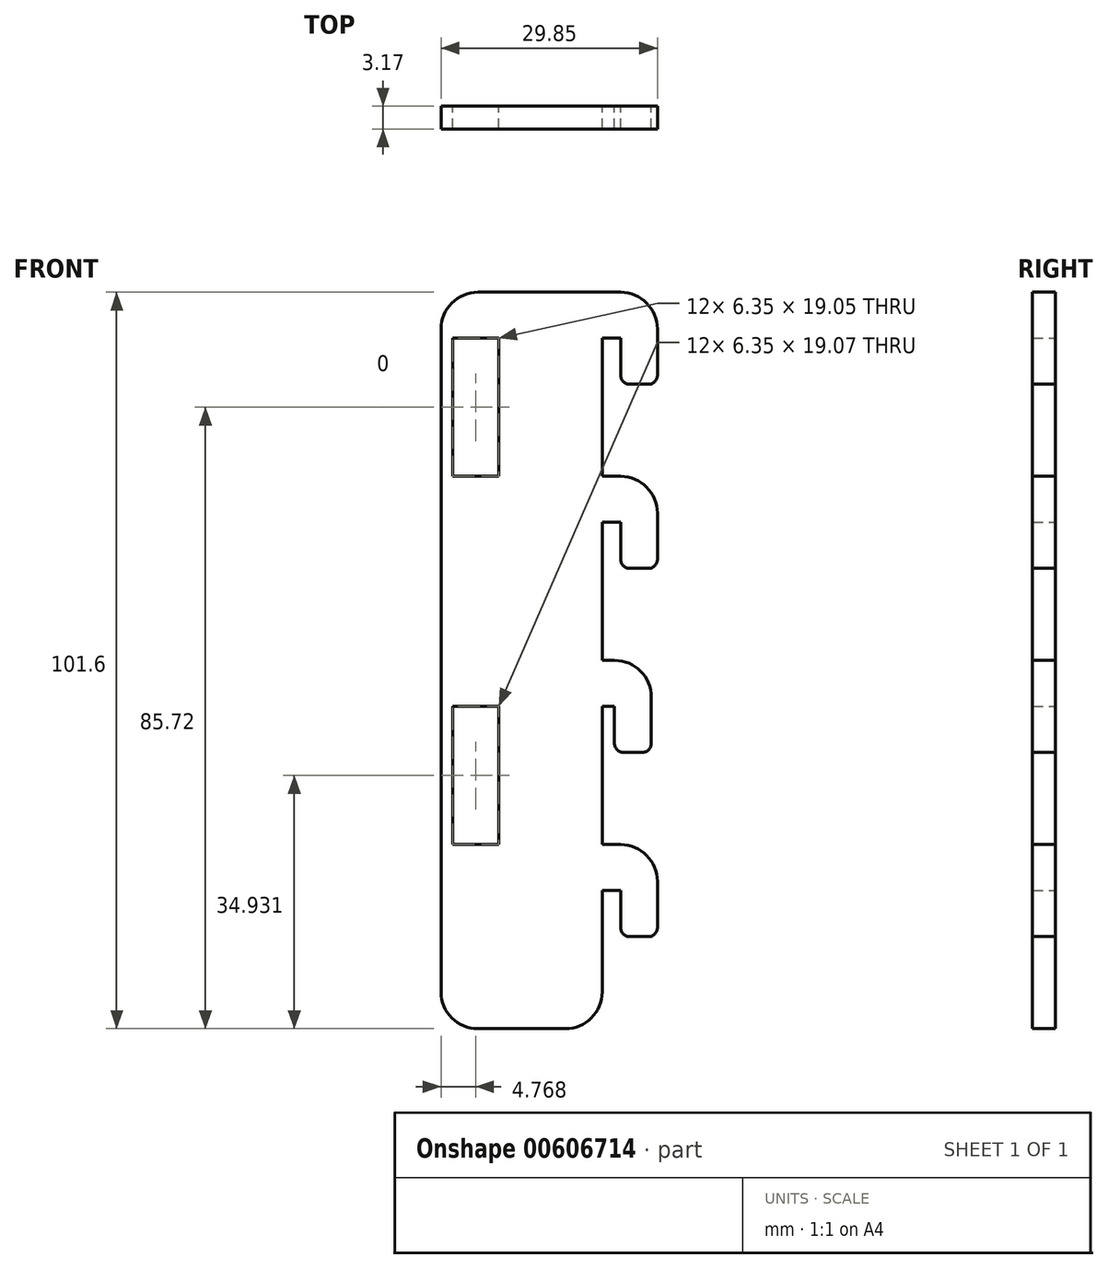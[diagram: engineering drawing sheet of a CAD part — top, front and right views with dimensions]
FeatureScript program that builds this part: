
annotation { "Feature Type Name" : "Feature", "Feature Type Description" : "" }
export const myFeature = defineFeature(function(context is Context, id is Id, definition is map)
    precondition{}
    {
        {
            var Q0;
            Q0=qCreatedBy(makeId("Front.planeOp"),FACE);
            var sketch = newSketch(context, id + "F0", { "sketchPlane" : qUnion([Q0])});
            skLineSegment(sketch, "E0", {"start": v(0, 56.94) * mm, "end": v(0, -44.66) * mm});
            skLineSegment(sketch, "E1", {"start": v(0, 56.94) * mm, "end": v(7.62, 56.94) * mm});
            skLineSegment(sketch, "E2", {"start": v(7.62, 56.94) * mm, "end": v(7.62, 44.24) * mm});
            skLineSegment(sketch, "E3", {"start": v(7.62, 44.24) * mm, "end": v(2.54, 44.24) * mm});
            skLineSegment(sketch, "E4", {"start": v(2.54, 44.24) * mm, "end": v(2.54, 50.59) * mm});
            skLineSegment(sketch, "E5", {"start": v(2.54, 50.59) * mm, "end": v(0, 50.59) * mm});
            skLineSegment(sketch, "E6", {"start": v(0, 56.94) * mm, "end": v(-12.7, 56.94) * mm});
            skLineSegment(sketch, "E7", {"start": v(-12.7, 56.94) * mm, "end": v(-12.7, -44.66) * mm});
            skLineSegment(sketch, "E8", {"start": v(-12.7, -44.66) * mm, "end": v(0, -44.66) * mm});
            skLineSegment(sketch, "E9", {"start": v(0, 56.94) * mm, "end": v(0, 31.54) * mm});
            skLineSegment(sketch, "E10", {"start": v(0, 31.54) * mm, "end": v(7.62, 31.54) * mm});
            skLineSegment(sketch, "E11", {"start": v(7.62, 31.54) * mm, "end": v(7.62, 18.84) * mm});
            skLineSegment(sketch, "E12", {"start": v(7.62, 18.84) * mm, "end": v(2.54, 18.84) * mm});
            skLineSegment(sketch, "E13", {"start": v(2.54, 18.84) * mm, "end": v(2.54, 25.19) * mm});
            skLineSegment(sketch, "E14", {"start": v(2.54, 25.19) * mm, "end": v(0, 25.19) * mm});
            skLineSegment(sketch, "E15", {"start": v(0, 31.54) * mm, "end": v(0, 0) * mm});
            skLineSegment(sketch, "E16", {"start": v(0, 31.54) * mm, "end": v(0, 6.14) * mm});
            skLineSegment(sketch, "E17", {"start": v(0, 6.14) * mm, "end": v(0, -19.26) * mm});
            skLineSegment(sketch, "E18", {"start": v(0, -19.26) * mm, "end": v(0, -44.66) * mm});
            skLineSegment(sketch, "E19", {"start": v(-0.85, 6.16) * mm, "end": v(6.77, 6.16) * mm});
            skLineSegment(sketch, "E20", {"start": v(6.77, 6.16) * mm, "end": v(6.77, -6.54) * mm});
            skLineSegment(sketch, "E21", {"start": v(6.77, -6.54) * mm, "end": v(1.7, -6.54) * mm});
            skLineSegment(sketch, "E22", {"start": v(1.7, -6.54) * mm, "end": v(1.7, -0.2) * mm});
            skLineSegment(sketch, "E23", {"start": v(1.7, -0.2) * mm, "end": v(-0.85, -0.2) * mm});
            skLineSegment(sketch, "E24", {"start": v(0, -19.26) * mm, "end": v(7.62, -19.26) * mm});
            skLineSegment(sketch, "E25", {"start": v(7.62, -19.26) * mm, "end": v(7.62, -31.96) * mm});
            skLineSegment(sketch, "E26", {"start": v(7.62, -31.96) * mm, "end": v(2.54, -31.96) * mm});
            skLineSegment(sketch, "E27", {"start": v(2.54, -31.96) * mm, "end": v(2.54, -25.61) * mm});
            skLineSegment(sketch, "E28", {"start": v(2.54, -25.61) * mm, "end": v(0, -25.61) * mm});
            skLineSegment(sketch, "E29", {"start": v(-12.7, 56.94) * mm, "end": v(-22.22, 56.94) * mm});
            skLineSegment(sketch, "E30", {"start": v(-22.22, 56.94) * mm, "end": v(-22.22, -44.66) * mm});
            skLineSegment(sketch, "E31", {"start": v(-22.22, -44.66) * mm, "end": v(-12.7, -44.66) * mm});
            skLineSegment(sketch, "E32", {"start": v(-17.46, -44.66) * mm, "end": v(-17.46, 56.94) * mm});
            skPoint(sketch, "E32.startSnap0", {"position": v(-17.46, 56.94) * mm});
            skLineSegment(sketch, "E33", {"start": v(-17.46, 50.59) * mm, "end": v(-14.29, 50.59) * mm});
            skLineSegment(sketch, "E34", {"start": v(-14.29, 50.59) * mm, "end": v(-14.29, 31.54) * mm});
            skLineSegment(sketch, "E35", {"start": v(-14.29, 31.54) * mm, "end": v(-20.64, 31.54) * mm});
            skLineSegment(sketch, "E36", {"start": v(-20.64, 31.54) * mm, "end": v(-20.64, 50.59) * mm});
            skLineSegment(sketch, "E37", {"start": v(-20.64, 50.59) * mm, "end": v(-17.46, 50.59) * mm});
            skLineSegment(sketch, "E38", {"start": v(-20.64, -0.2) * mm, "end": v(-14.29, -0.2) * mm});
            skPoint(sketch, "E38.endSnap0", {"position": v(0.42, -0.2) * mm});
            skLineSegment(sketch, "E39", {"start": v(-14.29, -0.2) * mm, "end": v(-14.29, -19.26) * mm});
            skLineSegment(sketch, "E40", {"start": v(-14.29, -19.26) * mm, "end": v(-20.64, -19.24) * mm});
            skLineSegment(sketch, "E41", {"start": v(-20.64, -19.24) * mm, "end": v(-20.64, -0.2) * mm});
            skSolve(sketch);
        }
        {
            var Q0;
            {var subQ7=sQuery(id+"F0.wireOp",EDGE,"E6");Q0=makeQuery(id+"F0.imprint","IMPRINT",FACE,{"disambiguationData":[TD([[makeQuery(id+"F0.imprint","IMPRINT",EDGE,{"derivedFrom":subQ7}),1.0]])]});}
            var Q1;
            {var subQ0=sQuery(id+"F0.wireOp",EDGE,"E1");Q1=makeQuery(id+"F0.imprint","IMPRINT",FACE,{"disambiguationData":[TD([[makeQuery(id+"F0.imprint","IMPRINT",EDGE,{"derivedFrom":subQ0}),-1.0]])]});}
            var Q2;
            {var subQ0=sQuery(id+"F0.wireOp",EDGE,"E10");Q2=makeQuery(id+"F0.imprint","IMPRINT",FACE,{"disambiguationData":[TD([[makeQuery(id+"F0.imprint","IMPRINT",EDGE,{"derivedFrom":subQ0}),-1.0]])]});}
            var Q3;
            {var subQ0=sQuery(id+"F0.wireOp",EDGE,"E20");Q3=makeQuery(id+"F0.imprint","IMPRINT",FACE,{"disambiguationData":[TD([[makeQuery(id+"F0.imprint","IMPRINT",EDGE,{"derivedFrom":subQ0}),-1.0]])]});}
            var Q4;
            {var subQ0=sQuery(id+"F0.wireOp",EDGE,"E24");Q4=makeQuery(id+"F0.imprint","IMPRINT",FACE,{"disambiguationData":[TD([[makeQuery(id+"F0.imprint","IMPRINT",EDGE,{"derivedFrom":subQ0}),-1.0]])]});}
            var Q5;
            {var subQ8=sQuery(id+"F0.wireOp",EDGE,"E7");Q5=makeQuery(id+"F0.imprint","IMPRINT",FACE,{"disambiguationData":[TD([[makeQuery(id+"F0.imprint","IMPRINT",EDGE,{"derivedFrom":subQ8}),-1.0]])]});}
            var Q6;
            {var subQ10=sQuery(id+"F0.wireOp",EDGE,"E30");Q6=makeQuery(id+"F0.imprint","IMPRINT",FACE,{"disambiguationData":[TD([[makeQuery(id+"F0.imprint","IMPRINT",EDGE,{"derivedFrom":subQ10}),1.0]])]});}
            extrude(context, id + "F1", {"entities" : qUnion([Q0, Q1, Q2, Q3, Q4, Q5, Q6]), "depth" : 3.17 * mm, "offsetDistance" : 25.4 * mm});
        }
        {
            var Q0;
            Q0=makeQuery(id+"F1.opExtrude","SWEPT_EDGE",EDGE,{"disambiguationData":[OSD([sQuery(id+"F0.wireOp",EDGE,"E29"),sQuery(id+"F0.wireOp",EDGE,"E30")])]});
            var Q1;
            Q1=makeQuery(id+"F1.opExtrude","SWEPT_EDGE",EDGE,{"disambiguationData":[OSD([sQuery(id+"F0.wireOp",EDGE,"E30"),sQuery(id+"F0.wireOp",EDGE,"E31")])]});
            var Q2;
            Q2=makeQuery(id+"F1.opExtrude","SWEPT_EDGE",EDGE,{"disambiguationData":[OSD([sQuery(id+"F0.wireOp",EDGE,"E8"),sQuery(id+"F0.wireOp",EDGE,"E18")])]});
            fillet(context, id + "F2", {"entities" : qUnion([Q0, Q1, Q2]), "radius" : 5.08 * mm, "tangentPropagation" : true, "allowEdgeOverflow" : false});
        }
        {
            var Q0;
            Q0=makeQuery(id+"F1.opExtrude","SWEPT_EDGE",EDGE,{"disambiguationData":[OSD([sQuery(id+"F0.wireOp",EDGE,"E10"),sQuery(id+"F0.wireOp",EDGE,"E11")])]});
            var Q1;
            Q1=makeQuery(id+"F1.opExtrude","SWEPT_EDGE",EDGE,{"disambiguationData":[OSD([sQuery(id+"F0.wireOp",EDGE,"E19"),sQuery(id+"F0.wireOp",EDGE,"E20")])]});
            var Q2;
            Q2=makeQuery(id+"F1.opExtrude","SWEPT_EDGE",EDGE,{"disambiguationData":[OSD([sQuery(id+"F0.wireOp",EDGE,"E24"),sQuery(id+"F0.wireOp",EDGE,"E25")])]});
            var Q3;
            Q3=makeQuery(id+"F1.opExtrude","SWEPT_EDGE",EDGE,{"disambiguationData":[OSD([sQuery(id+"F0.wireOp",EDGE,"E1"),sQuery(id+"F0.wireOp",EDGE,"E2")])]});
            fillet(context, id + "F3", {"entities" : qUnion([Q0, Q1, Q2, Q3]), "radius" : 5.08 * mm, "tangentPropagation" : true, "allowEdgeOverflow" : false});
        }
        {
            var Q0;
            Q0=makeQuery(id+"F1.opExtrude","SWEPT_EDGE",EDGE,{"disambiguationData":[OSD([sQuery(id+"F0.wireOp",EDGE,"E11"),sQuery(id+"F0.wireOp",EDGE,"E12")])]});
            var Q1;
            Q1=makeQuery(id+"F1.opExtrude","SWEPT_EDGE",EDGE,{"disambiguationData":[OSD([sQuery(id+"F0.wireOp",EDGE,"E12"),sQuery(id+"F0.wireOp",EDGE,"E13")])]});
            var Q2;
            Q2=makeQuery(id+"F1.opExtrude","SWEPT_EDGE",EDGE,{"disambiguationData":[OSD([sQuery(id+"F0.wireOp",EDGE,"E20"),sQuery(id+"F0.wireOp",EDGE,"E21")])]});
            var Q3;
            Q3=makeQuery(id+"F1.opExtrude","SWEPT_EDGE",EDGE,{"disambiguationData":[OSD([sQuery(id+"F0.wireOp",EDGE,"E21"),sQuery(id+"F0.wireOp",EDGE,"E22")])]});
            var Q4;
            Q4=makeQuery(id+"F1.opExtrude","SWEPT_EDGE",EDGE,{"disambiguationData":[OSD([sQuery(id+"F0.wireOp",EDGE,"E3"),sQuery(id+"F0.wireOp",EDGE,"E4")])]});
            var Q5;
            Q5=makeQuery(id+"F1.opExtrude","SWEPT_EDGE",EDGE,{"disambiguationData":[OSD([sQuery(id+"F0.wireOp",EDGE,"E2"),sQuery(id+"F0.wireOp",EDGE,"E3")])]});
            var Q6;
            Q6=makeQuery(id+"F1.opExtrude","SWEPT_EDGE",EDGE,{"disambiguationData":[OSD([sQuery(id+"F0.wireOp",EDGE,"E25"),sQuery(id+"F0.wireOp",EDGE,"E26")])]});
            var Q7;
            Q7=makeQuery(id+"F1.opExtrude","SWEPT_EDGE",EDGE,{"disambiguationData":[OSD([sQuery(id+"F0.wireOp",EDGE,"E26"),sQuery(id+"F0.wireOp",EDGE,"E27")])]});
            fillet(context, id + "F4", {"entities" : qUnion([Q0, Q1, Q2, Q3, Q4, Q5, Q6, Q7]), "radius" : 1.27 * mm, "tangentPropagation" : true, "allowEdgeOverflow" : false});
        }
    });
